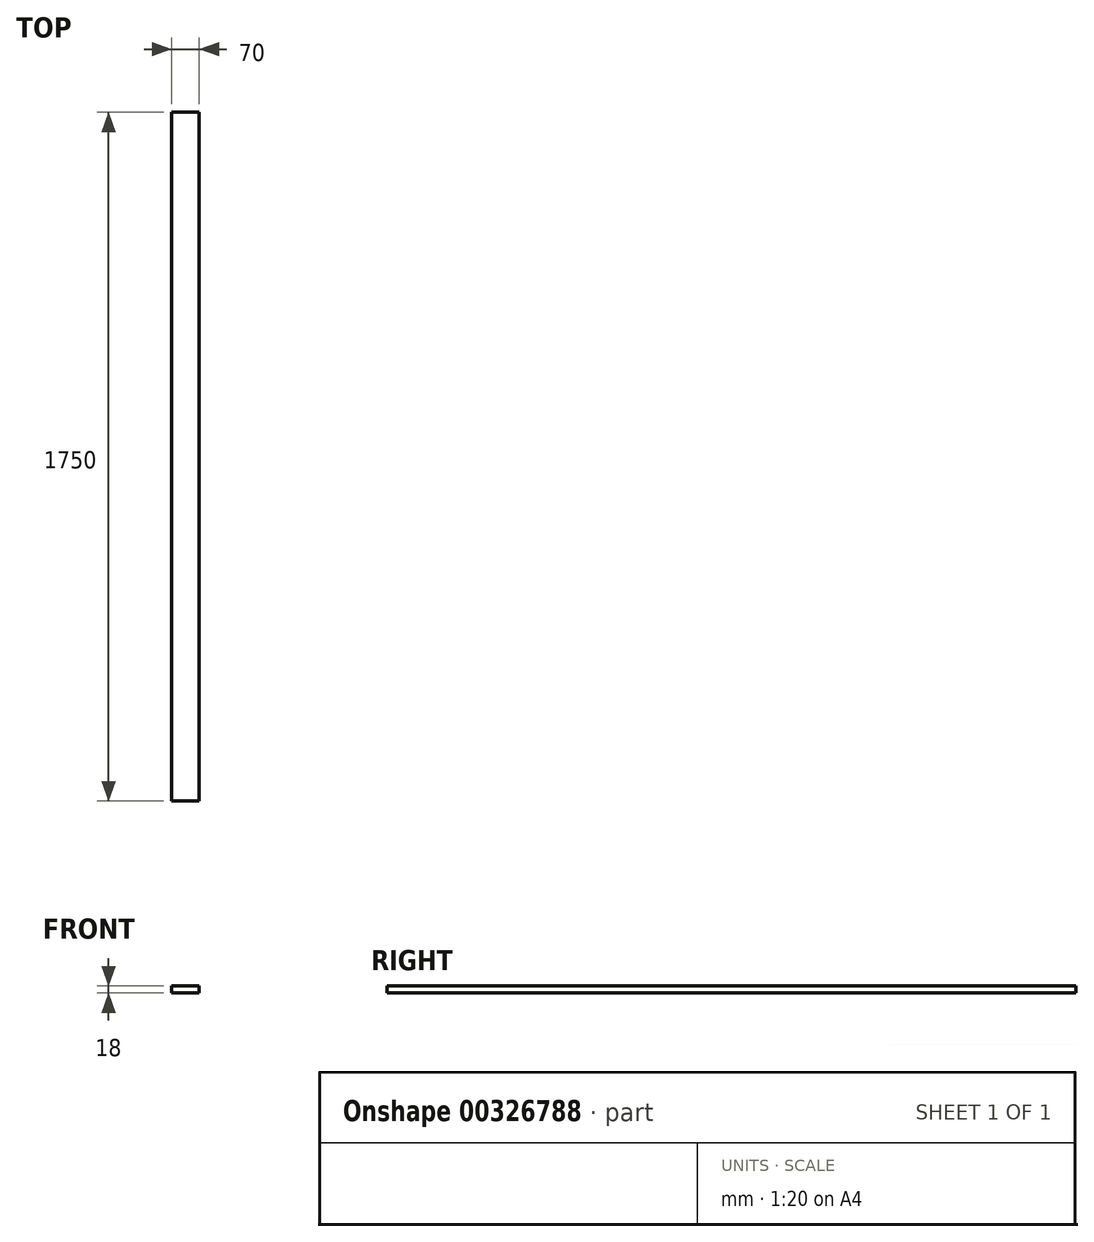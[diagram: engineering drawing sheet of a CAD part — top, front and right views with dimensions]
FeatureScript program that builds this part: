
annotation { "Feature Type Name" : "Feature", "Feature Type Description" : "" }
export const myFeature = defineFeature(function(context is Context, id is Id, definition is map)
    precondition{}
    {
        {
            var Q0;
            Q0=qCreatedBy(makeId("Top.planeOp"),FACE);
            var sketch = newSketch(context, id + "F0", { "sketchPlane" : qUnion([Q0])});
            skLineSegment(sketch, "E0.bottom", {"start": v(0, 0) * mm, "end": v(70, 0) * mm});
            skLineSegment(sketch, "E0.top", {"start": v(0, 1750) * mm, "end": v(70, 1750) * mm});
            skLineSegment(sketch, "E0.left", {"start": v(0, 0) * mm, "end": v(0, 1750) * mm});
            skLineSegment(sketch, "E0.right", {"start": v(70, 0) * mm, "end": v(70, 1750) * mm});
            skSolve(sketch);
        }
        {
            var Q0;
            Q0=qSketchRegion(id+"F0",true);
            extrude(context, id + "F1", {"entities" : qUnion([Q0]), "depth" : 18 * mm});
        }
    });
